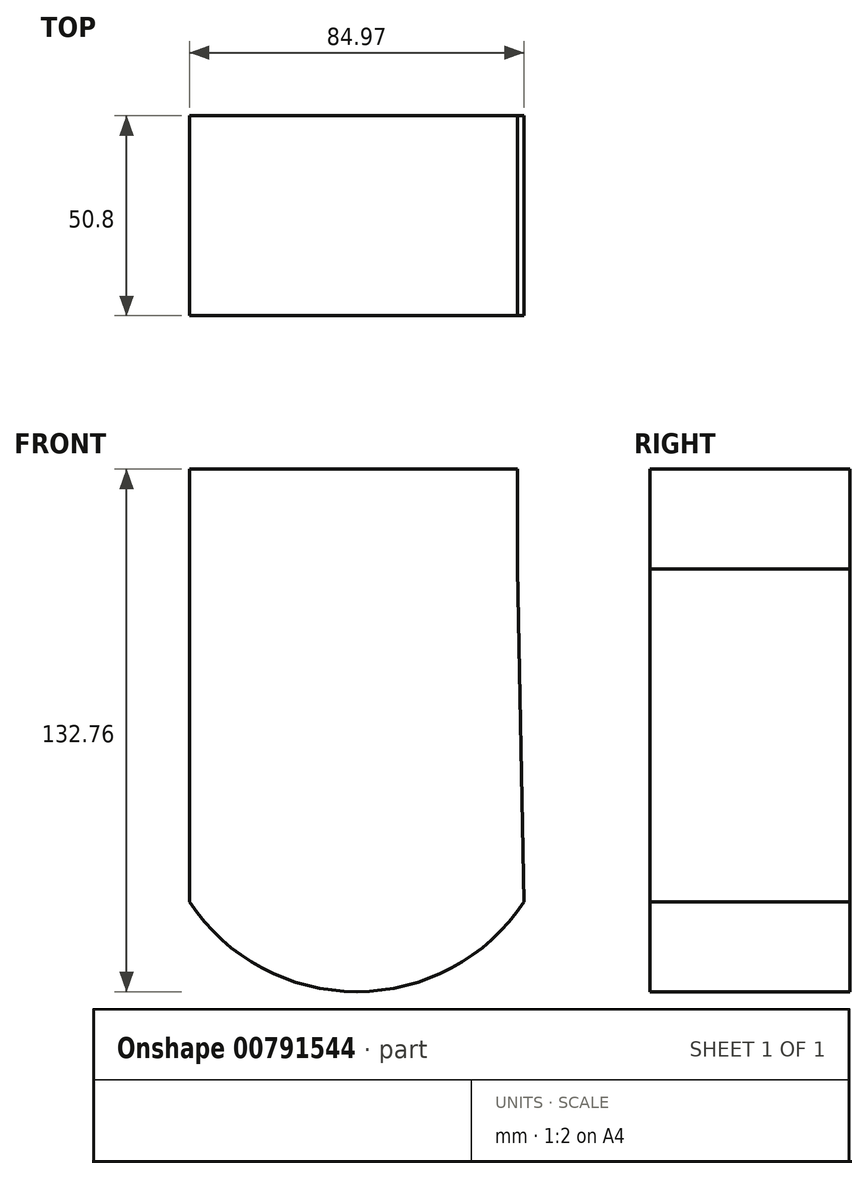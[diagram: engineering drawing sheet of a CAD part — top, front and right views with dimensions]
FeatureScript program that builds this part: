
annotation { "Feature Type Name" : "Feature", "Feature Type Description" : "" }
export const myFeature = defineFeature(function(context is Context, id is Id, definition is map)
    precondition{}
    {
        {
            var Q0;
            Q0=qCreatedBy(makeId("Front.planeOp"),FACE);
            var sketch = newSketch(context, id + "F0", { "sketchPlane" : qUnion([Q0])});
            skLineSegment(sketch, "E0", {"start": v(-49.17, 34.09) * mm, "end": v(34.09, 34.09) * mm});
            skPoint(sketch, "E1.end.orphan", {"position": v(-49.17, -50.5) * mm});
            skLineSegment(sketch, "E2", {"start": v(-49.17, 34.09) * mm, "end": v(-49.17, -50.5) * mm});
            skLineSegment(sketch, "E3", {"start": v(34.09, 34.09) * mm, "end": v(35.8, -50.5) * mm});
            skArc(sketch, "E4", {"start": v(-49.17, -50.5) * mm, "mid": v(-6.68, -73.27) * mm, "end": v(35.8, -50.5) * mm});
            skSolve(sketch);
        }
        {
            var Q0;
            Q0=makeQuery(id+"F0.imprint","IMPRINT",FACE,{"disambiguationData":[TD([[makeQuery(id+"F0.imprint","IMPRINT",EDGE,{"derivedFrom":sQuery(id+"F0.wireOp",EDGE,"E0")}),-1.0]])]});
            extrude(context, id + "F1", {"entities" : qUnion([Q0]), "depth" : 50.8 * mm, "offsetDistance" : 25.4 * mm});
        }
        {
            var Q0;
            Q0=makeQuery(id+"F1.opExtrude","SWEPT_FACE",FACE,{"disambiguationData":[OSD([sQuery(id+"F0.wireOp",EDGE,"E0")])]});
            extrude(context, id + "F2", {"entities" : qUnion([Q0]), "operationType" : NewBodyOperationType.ADD, "depth" : 25.4 * mm, "offsetDistance" : 25.4 * mm});
        }
    });
